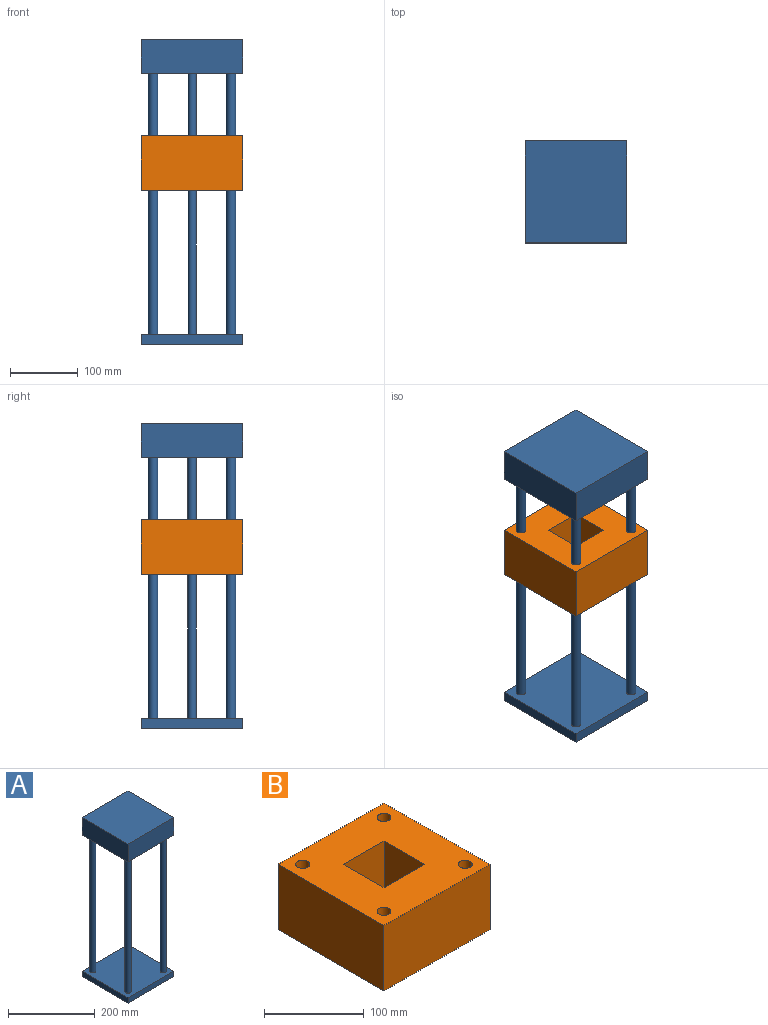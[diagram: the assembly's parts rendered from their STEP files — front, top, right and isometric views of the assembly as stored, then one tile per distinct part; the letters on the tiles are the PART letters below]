
ASSEMBLY  parts=2 mates=1
PART A: 17 faces, bbox 150x150x450 mm
  f0: plane 150x15mm, normal (1,0,0), area 2250mm2, adj f1,f3,f4,f5
  f1: plane 150x15mm, normal (0,1,0), area 2250mm2, adj f0,f2,f4,f5
  f2: plane 150x15mm, normal (-1,0,0), area 2250mm2, adj f1,f3,f4,f5
  f3: plane 150x15mm, normal (0,-1,0), area 2250mm2, adj f0,f2,f4,f5
  f4: plane 150x150mm, normal (0,0,1), area 21771.2mm2, adj f0,f1,f2,f3,f6,f7,f8,f9
  f5: plane 150x150mm, normal (0,0,-1), area 22500mm2, adj f0,f1,f2,f3
  f6: cylinder r=7mm len=385mm, axis (0,0,-1), area 16933.2mm2, adj f4,f10
  f7: cylinder r=7mm len=385mm, axis (0,0,-1), area 16933.2mm2, adj f4,f10
  f8: cylinder r=7mm len=385mm, axis (0,0,-1), area 16933.2mm2, adj f4,f10
  f9: cylinder r=7mm len=385mm, axis (0,0,-1), area 16933.2mm2, adj f4,f10
  f10: plane 150x150mm, normal (0,0,-1), area 21771.2mm2, adj f6,f7,f8,f9,f12,f13,f14,f15
  f11: plane 150x150mm, normal (0,0,1), area 22500mm2, adj f12,f13,f14,f15
  f12: plane 150x50mm, normal (1,0,0), area 7500mm2, adj f10,f11,f13,f15
  f13: plane 150x50mm, normal (0,1,0), area 7500mm2, adj f10,f11,f12,f14
  f14: plane 150x50mm, normal (-1,0,0), area 7500mm2, adj f10,f11,f13,f15
  f15: plane 150x50mm, normal (0,-1,0), area 7500mm2, adj f10,f11,f12,f14
  f16: cylinder r=6mm len=385mm, axis (0,0,-1), area 14514.2mm2, adj f4,f10
PART B: 14 faces, bbox 150x150x80 mm
  f0: plane 80x57mm, normal (0,-1,0), area 4560mm2, adj f1,f11,f12,f13
  f1: plane 80x57mm, normal (-1,0,0), area 4560mm2, adj f0,f2,f12,f13
  f2: plane 80x57mm, normal (0,1,0), area 4560mm2, adj f1,f11,f12,f13
  f3: plane 150x80mm, normal (1,0,0), area 12000mm2, adj f4,f10,f12,f13
  f4: plane 150x80mm, normal (0,1,0), area 12000mm2, adj f3,f5,f12,f13
  f5: plane 150x80mm, normal (-1,0,0), area 12000mm2, adj f4,f10,f12,f13
  f6: cylinder r=7mm len=80mm, axis (0,0,1), area 3518.6mm2, adj f12,f13
  f7: cylinder r=7mm len=80mm, axis (0,0,1), area 3518.6mm2, adj f12,f13
  f8: cylinder r=7mm len=80mm, axis (0,0,1), area 3518.6mm2, adj f12,f13
  f9: cylinder r=7mm len=80mm, axis (0,0,1), area 3518.6mm2, adj f12,f13
  f10: plane 150x80mm, normal (0,-1,0), area 12000mm2, adj f3,f5,f12,f13
  f11: plane 80x57mm, normal (1,0,0), area 4560mm2, adj f0,f2,f12,f13
  f12: plane 150x150mm, normal (0,0,-1), area 18635.2mm2, adj f0,f1,f2,f3,f4,f5,f6,f7
  f13: plane 150x150mm, normal (0,0,1), area 18635.2mm2, adj f0,f1,f2,f3,f4,f5,f6,f7
PLACE A t=(-276.9,-18.34,290.28)mm
PLACE B t=(-276.9,-18.34,598.06)mm fixed
MATE slider B.f9 <-> A.f7  axis (0,0,1) through (-219.4,-75.84,598.06)mm
